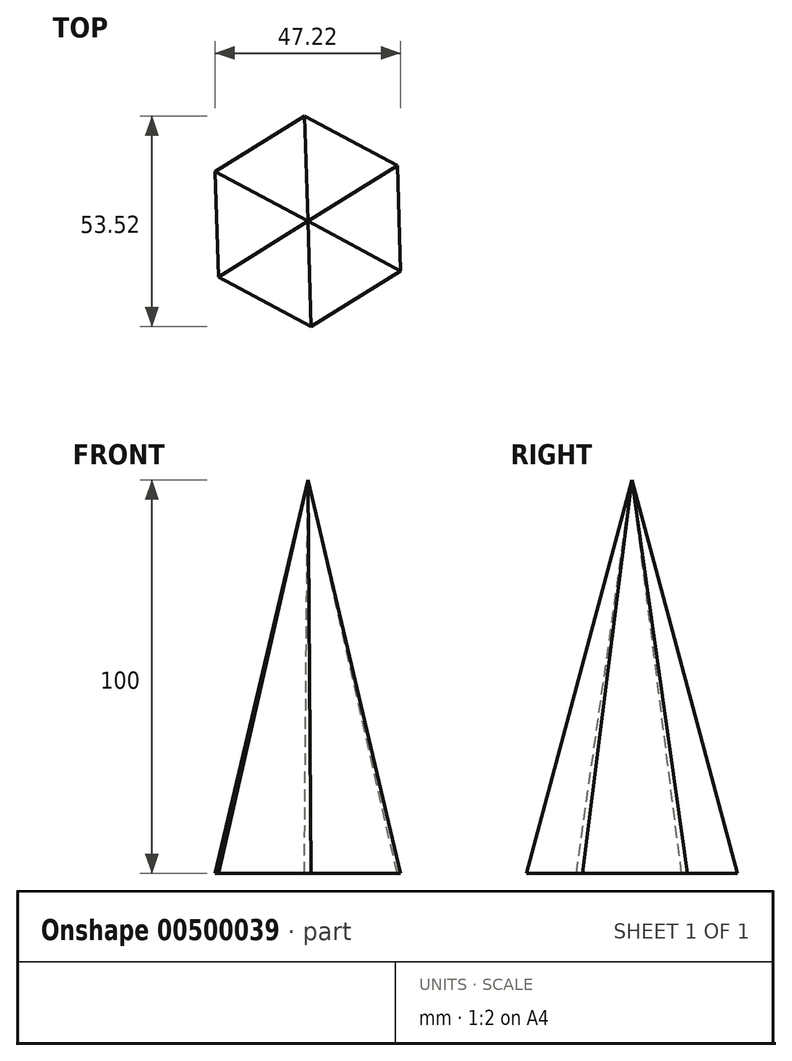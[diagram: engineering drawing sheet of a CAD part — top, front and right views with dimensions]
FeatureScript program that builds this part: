
annotation { "Feature Type Name" : "Feature", "Feature Type Description" : "" }
export const myFeature = defineFeature(function(context is Context, id is Id, definition is map)
    precondition{}
    {
        {
            var Q0;
            Q0=qCreatedBy(makeId("Top.planeOp"),FACE);
            var sketch = newSketch(context, id + "F0", { "sketchPlane" : qUnion([Q0])});
            skCircle(sketch, "E0.cCircle", {"center": v(0, 0) * mm, "radius": 26.77 * mm, "construction": true});
            skLineSegment(sketch, "E0.0", {"start": v(22.74, 14.14) * mm, "end": v(23.61, -12.62) * mm});
            skLineSegment(sketch, "E0.1", {"start": v(23.61, -12.62) * mm, "end": v(0.88, -26.76) * mm});
            skLineSegment(sketch, "E0.2", {"start": v(0.88, -26.76) * mm, "end": v(-22.74, -14.14) * mm});
            skLineSegment(sketch, "E0.3", {"start": v(-22.74, -14.14) * mm, "end": v(-23.61, 12.62) * mm});
            skLineSegment(sketch, "E0.4", {"start": v(-23.61, 12.62) * mm, "end": v(-0.88, 26.76) * mm});
            skLineSegment(sketch, "E0.5", {"start": v(-0.88, 26.76) * mm, "end": v(22.74, 14.14) * mm});
            skSolve(sketch);
        }
        {
            var Q0;
            Q0=qCreatedBy(makeId("Top.planeOp"),FACE);
            cPlane(context, id + "F1", {"entities" : qUnion([Q0]), "cplaneType" : CPlaneType.OFFSET, "offset" : 100 * mm, "width" : 152.4 * mm, "height" : 152.4 * mm});
        }
        {
            var Q0;
            Q0=qCreatedBy(id+"F1.planeOp",FACE);
            var sketch = newSketch(context, id + "F2", { "sketchPlane" : qUnion([Q0])});
            skPoint(sketch, "E1", {"position": v(0, 0) * mm});
            skSolve(sketch);
        }
        {
            var Q0;
            Q0=makeQuery(id+"F0.imprint","IMPRINT",FACE,{"disambiguationData":[TD([[makeQuery(id+"F0.imprint","IMPRINT",EDGE,{"derivedFrom":sQuery(id+"F0.wireOp",EDGE,"E0.0")}),-1.0]])]});
            var Q1;
            Q1=sQuery(id+"F2.wireOp",VERTEX,"E1");
            loft(context, id + "F3", {"sheetProfilesArray" : [{ "sheetProfileEntities" : qUnion([Q0]) }, { "sheetProfileEntities" : qUnion([Q1]) }]});
        }
    });
